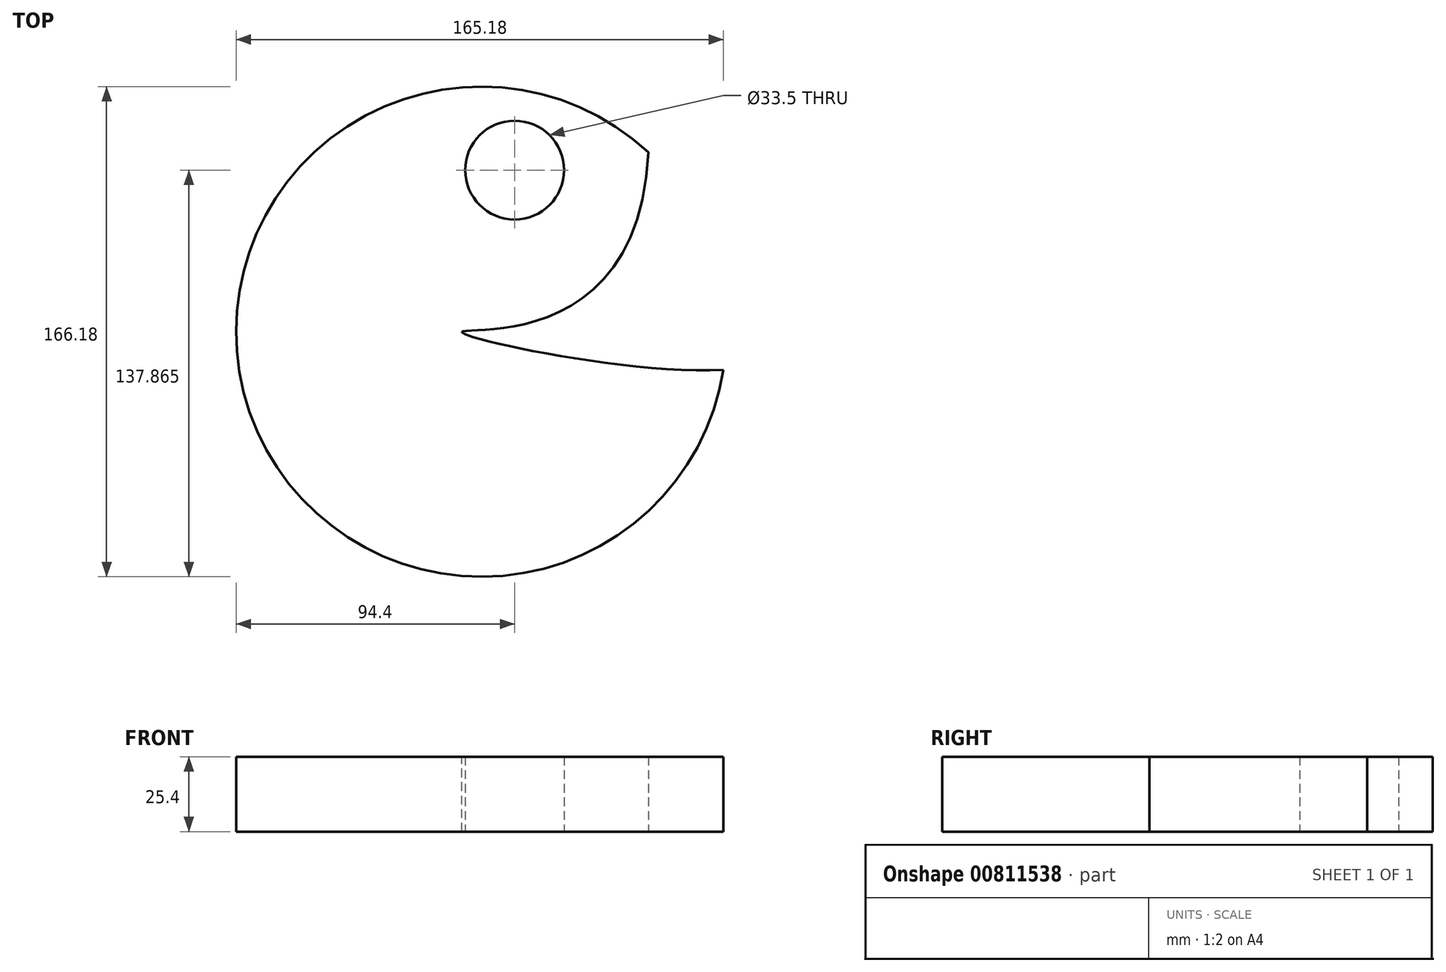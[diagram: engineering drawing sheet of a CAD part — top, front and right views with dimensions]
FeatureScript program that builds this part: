
annotation { "Feature Type Name" : "Feature", "Feature Type Description" : "" }
export const myFeature = defineFeature(function(context is Context, id is Id, definition is map)
    precondition{}
    {
        {
            var Q0;
            Q0=qCreatedBy(makeId("Top.planeOp"),FACE);
            var sketch = newSketch(context, id + "F0", { "sketchPlane" : qUnion([Q0])});
            skArc(sketch, "E0", {"start": v(56.62, 60.82) * mm, "mid": v(-78.54, -27.13) * mm, "end": v(82.09, -12.9) * mm});
            skFitSpline(sketch, "E1", {"points": [v(56.62, 60.82) * mm, v(-6.59, 0) * mm, v(82.09, -12.9) * mm], "startDerivative": vector(-18.93, -407.66) * mm, "endDerivative": vector(202.12, 10.56) * mm});
            skCircle(sketch, "E2", {"center": v(11.31, 54.78) * mm, "radius": 16.75 * mm});
            skLineSegment(sketch, "E3", {"start": v(-6.59, 0) * mm, "end": v(-83.1, 0) * mm});
            skSolve(sketch);
        }
        {
            var Q0;
            Q0=makeQuery(id+"F0.imprint","IMPRINT",FACE,{"disambiguationData":[TD([[makeQuery(id+"F0.imprint","IMPRINT",EDGE,{"derivedFrom":sQuery(id+"F0.wireOp",EDGE,"E2")}),-1.0]])]});
            var Q1;
            {var subQ0=sQuery(id+"F0.wireOp",EDGE,"E1");var subQ1=sQuery(id+"F0.wireOp",EDGE,"E0");var subQ2=makeQuery(id+"F0.imprint","INTERSECT",VERTEX,{"disambiguationData":[OD(1.0)],"derivedFrom":[subQ1,subQ0]});Q1=makeQuery(id+"F0.imprint","IMPRINT",FACE,{"disambiguationData":[TD([[makeQuery(id+"F0.imprint","IMPRINT",EDGE,{"disambiguationData":[TD([[subQ2,1.0]])],"derivedFrom":subQ1}),1.0]])]});}
            extrude(context, id + "F1", {"entities" : qUnion([Q0, Q1]), "depth" : 25.4 * mm, "offsetDistance" : 25.4 * mm});
        }
    });
